# Revit family: 111213058021734
name_source: partatom
category: Modelos genéricos
revit_build: Autodesk Revit 2018 (Build: 20190510_1515(x64)
units: mm (PartAtom-declared; Revit-internal decimal feet)

## family parameters
Compartido = No
Corte con vacíos al cargar = No
Cota de conector redondo = Diámetro de uso
Puede alojar armadura = No
Punto de cálculo de habitación = No
Se basa en plano de trabajo = No
Siempre vertical = No
Tipo de pieza = Normal

## types (1)
- DESCANSO NEO PVC 300MM GRIS TIRA 1.20
    Alto = 50 mm  [stored 0.164042 ft]
    Aplicacion = Escaleras
    Color = GRIS
    Descripción = Grada Neo 300x50 MM.
    Dimension = 300 mm
    Dureza = 80 shore A
    Empresa = CNP SPA.
    Espesor = 2 mm  [stored 0.00656168 ft]
    Largo = 1200 mm
    Material = PVC flexible gris
    Modelo = DESCANSO NEO PVC 300MM
    Nombre SKU = DESCANSO NEO PVC 300MM GRIS TIRA 1.2MT
    Num SKUs = 111213058021734
    URL = https://www.empresascnp.cl
    Unidad = Tiras de 1.20 Mts y 3.00 Mts.
    Url Ficha tecnica = https://empresascnp.cl
    Uso = Es un producto que se instala en los descansos de las escaleras, es una solución
fabricada en PVC, ideal para zonas de medio y alto trafico, con estrías antideslizantes.
Ideal para: Edificios Públicos y Privados, Colegios, Universidades, Centros comerciales,
Aeropuertos, Hoteles, Edificios Habitacionales, entre otros.
    Ventajas = Autoextinguible

note: [stored X ft] marks values corroborated as IEEE doubles in the binary element streams (Revit-internal decimal feet)

## geometry (parser evidence)
native form markers: Sweep x1
no freeform markers — native parametric forms only
